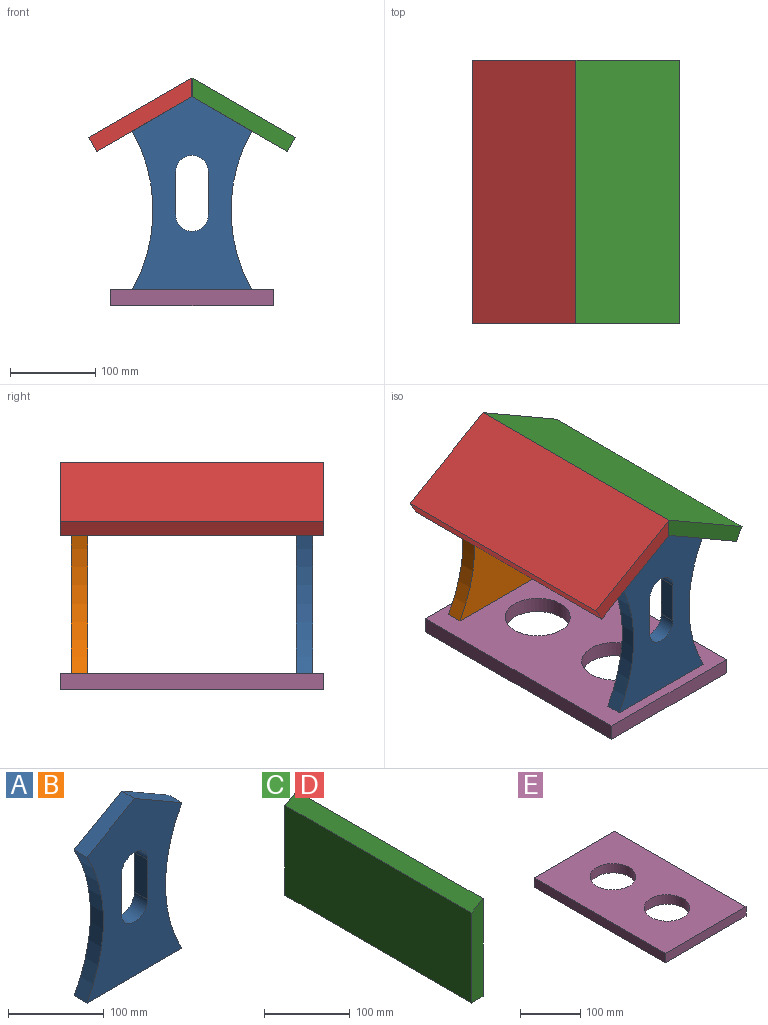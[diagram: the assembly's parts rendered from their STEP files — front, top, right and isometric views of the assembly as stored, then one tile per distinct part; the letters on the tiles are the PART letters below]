
ASSEMBLY  parts=5 mates=8
PART A: 11 faces, bbox 139.7x19.1x226 mm
  f0: plane 226.03x139.7mm, normal (0,1,0), area 19621.7mm2, adj f2,f3,f4,f5,f6,f7,f8,f9
  f1: plane 226.03x139.7mm, normal (0,-1,0), area 19621.7mm2, adj f2,f3,f4,f5,f6,f7,f8,f9
  f2: plane 139.7x19.05mm, normal (0,0,-1), area 2661.3mm2, adj f0,f1,f5,f6
  f3: plane 69.85x40.33mm, normal (0.5,0,0.87), area 1536.5mm2, adj f0,f1,f4,f6
  f4: plane 69.85x40.33mm, normal (-0.5,0,0.87), area 1536.5mm2, adj f0,f1,f3,f5
  f5: cylinder r=190.5mm len=185.71mm, axis (0,-1,0), area 3695.3mm2, adj f0,f1,f2,f4
  f6: cylinder r=190.5mm len=185.71mm, axis (0,-1,0), area 3695.3mm2, adj f0,f1,f2,f3
  f7: cylinder r=19.05mm len=38.1mm, axis (0,-1,0), area 1140.1mm2, adj f0,f1,f8,f9
  f8: plane 50.8x19.05mm, normal (-1,0,0), area 967.7mm2, adj f0,f1,f7,f10
  f9: plane 50.8x19.05mm, normal (1,0,0), area 967.7mm2, adj f0,f1,f7,f10
  f10: cylinder r=19.05mm len=38.1mm, axis (0,-1,0), area 1140.1mm2, adj f0,f1,f8,f9
PART B: same geometry as A
PART C: 6 faces, bbox 19.1x308.2x139.7 mm
  f0: plane 139.7x19.05mm, normal (0,-1,0), area 2556.5mm2, adj f1,f2,f4,f5
  f1: plane 308.23x128.7mm, normal (-1,0,0), area 39669.5mm2, adj f0,f2,f3,f5
  f2: plane 308.23x19.05mm, normal (0,0,-1), area 5871.8mm2, adj f0,f1,f3,f4
  f3: plane 139.7x19.05mm, normal (0,1,0), area 2556.5mm2, adj f1,f2,f4,f5
  f4: plane 308.23x139.7mm, normal (1,0,0), area 43059.6mm2, adj f0,f2,f3,f5
  f5: plane 308.23x19.05mm, normal (-0.5,0,0.87), area 6780.1mm2, adj f0,f1,f3,f4
PART D: same geometry as C
PART E: 8 faces, bbox 190.5x308.2x19.1 mm
  f0: plane 190.5x19.05mm, normal (0,-1,0), area 3629mm2, adj f1,f3,f4,f5
  f1: plane 308.23x19.05mm, normal (1,0,0), area 5871.8mm2, adj f0,f2,f4,f5
  f2: plane 190.5x19.05mm, normal (0,1,0), area 3629mm2, adj f1,f3,f4,f5
  f3: plane 308.23x19.05mm, normal (-1,0,0), area 5871.8mm2, adj f0,f2,f4,f5
  f4: plane 308.23x190.5mm, normal (0,0,1), area 49596.9mm2, adj f0,f1,f2,f3,f6,f7
  f5: plane 308.23x190.5mm, normal (0,0,-1), area 49596.9mm2, adj f0,f1,f2,f3,f6,f7
  f6: cylinder r=38.1mm len=76.2mm, axis (0,0,1), area 4560.4mm2, adj f4,f5
  f7: cylinder r=38.1mm len=76.2mm, axis (0,0,1), area 4560.4mm2, adj f4,f5
PLACE A t=(0,-131.89,113.02)mm
PLACE B t=(0,131.89,113.02)mm
PLACE C rot(axis=(0,-1,0),60deg) t=(55.73,0,204.86)mm
PLACE D rot(axis=(-0.5,0,-0.87),180deg) t=(-55.73,0,204.86)mm
PLACE E t=(0,0,-9.53)mm
MATE planar E.f0 <-> C.f0  axis (0,-1,0) through (95.25,-154.11,-9.53)mm
MATE planar A.f3 <-> C.f1  axis (0.5,0,0.87) through (34.92,-131.89,205.87)mm
MATE planar C.f0 <-> D.f3  axis (0,-1,0) through (60.49,-154.11,213.11)mm
MATE fastened E.f4 <-> A.f2  axis (0,0,1) through (0,-154.11,0)mm
MATE ball C.f0 <-> D.f5  axis (0,-1,0) through (0,-154.11,248.03)mm
MATE planar B.f4 <-> D.f1  axis (-0.5,0,0.87) through (-34.92,131.89,205.87)mm
MATE fastened E.f4 <-> B.f2  axis (0,0,1) through (0,154.11,0)mm
MATE planar D.f5 <-> C.f5  axis (1,0,0) through (0,0,237.03)mm
